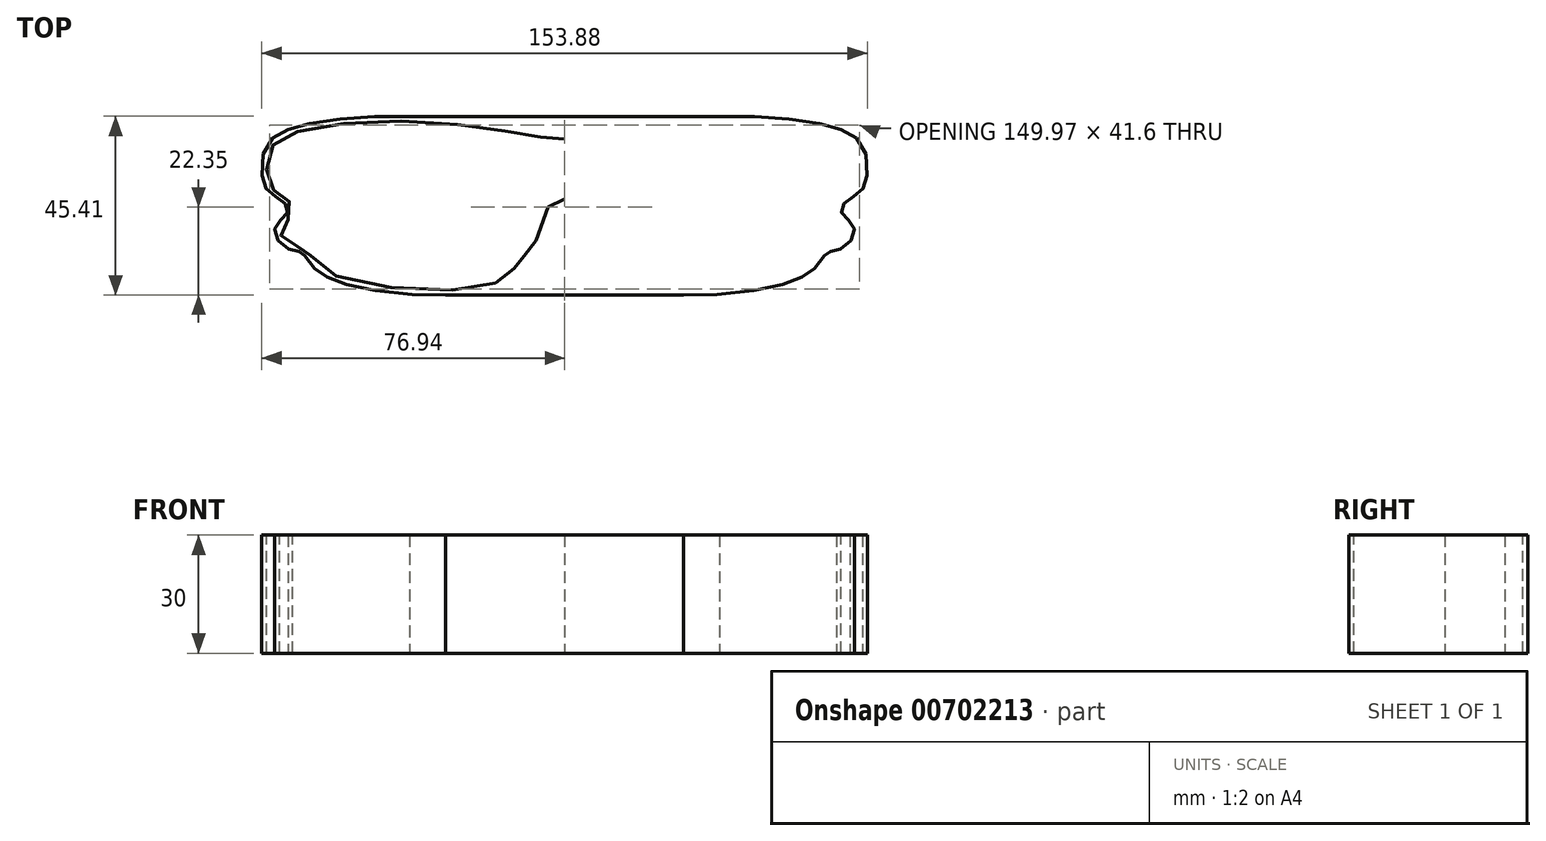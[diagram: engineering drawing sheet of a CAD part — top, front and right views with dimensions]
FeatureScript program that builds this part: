
annotation { "Feature Type Name" : "Feature", "Feature Type Description" : "" }
export const myFeature = defineFeature(function(context is Context, id is Id, definition is map)
    precondition{}
    {
        {
            var Q0;
            Q0=qCreatedBy(makeId("Top.planeOp"),FACE);
            var sketch = newSketch(context, id + "F0", { "sketchPlane" : qUnion([Q0])});
            skPoint(sketch, "E0", {"position": v(0, 65.63) * mm});
            skPoint(sketch, "E1", {"position": v(87.5, 0) * mm});
            skLineSegment(sketch, "E2", {"start": v(0, 89.37) * mm, "end": v(0, -72.57) * mm, "construction": true});
            skLineSegment(sketch, "E3", {"start": v(-93.15, 0) * mm, "end": v(109.27, 0) * mm, "construction": true});
            skLineSegment(sketch, "E4", {"start": v(36.39, -17.94) * mm, "end": v(36.39, 15.86) * mm, "construction": true});
            skFitSpline(sketch, "E5", {"points": [v(0, 16.42) * mm, v(-8.35, 17.29) * mm, v(-36.63, 20.8) * mm, v(-70.08, 17.58) * mm, v(-75.27, 12.4) * mm, v(-74.68, 4.18) * mm, v(-71.26, 1.93) * mm, v(-69.2, -2.67) * mm, v(-72.43, -6.58) * mm, v(-69.3, -10.6) * mm, v(-66.17, -11.28) * mm, v(-60.79, -17.05) * mm, v(-22.15, -21.36) * mm, v(-13.05, -16.95) * mm, v(-10.8, -13.53) * mm, v(-8.84, -12.65) * mm, v(-3.88, -0.47) * mm, v(0, 1.2) * mm], "startDerivative": vector(-129.58, 0) * mm, "endDerivative": vector(103.17, 3.03) * mm});
            skFitSpline(sketch, "E6.MirrorCS", {"points": [v(0, 16.42) * mm, v(8.35, 17.29) * mm, v(36.63, 20.8) * mm, v(70.08, 17.58) * mm, v(75.27, 12.4) * mm, v(74.68, 4.18) * mm, v(71.26, 1.93) * mm, v(69.2, -2.67) * mm, v(72.43, -6.58) * mm, v(69.3, -10.6) * mm, v(66.17, -11.28) * mm, v(60.79, -17.05) * mm, v(22.15, -21.36) * mm, v(13.05, -16.95) * mm, v(10.8, -13.53) * mm, v(8.84, -12.65) * mm, v(3.88, -0.47) * mm, v(0, 1.2) * mm], "startDerivative": vector(129.58, 0) * mm, "endDerivative": vector(-103.17, 3.03) * mm});
            skFitSpline(sketch, "E7.0", {"points": [v(0, 17.62) * mm, v(-0.65, 17.62) * mm, v(-1.94, 17.66) * mm, v(-4.04, 17.86) * mm, v(-6.04, 18.13) * mm, v(-7.86, 18.42) * mm, v(-9.86, 18.75) * mm, v(-12.67, 19.23) * mm, v(-16.5, 19.86) * mm, v(-20.74, 20.5) * mm, v(-25.33, 21.1) * mm, v(-30.22, 21.62) * mm, v(-35.38, 21.98) * mm, v(-40.74, 22.15) * mm, v(-46.18, 22.12) * mm, v(-51.54, 21.9) * mm, v(-56.68, 21.48) * mm, v(-61.46, 20.9) * mm, v(-65.01, 20.25) * mm, v(-67.54, 19.65) * mm, v(-69.26, 19.16) * mm, v(-70.8, 18.61) * mm, v(-72.13, 18) * mm, v(-73.3, 17.32) * mm, v(-74.29, 16.52) * mm, v(-75.12, 15.6) * mm, v(-75.98, 14.2) * mm, v(-76.64, 12.2) * mm, v(-76.92, 9.87) * mm, v(-76.9, 8) * mm, v(-76.78, 6.63) * mm, v(-76.56, 5.56) * mm, v(-76.31, 4.76) * mm, v(-76.08, 4.2) * mm, v(-75.8, 3.66) * mm, v(-75.44, 3.17) * mm, v(-75.04, 2.77) * mm, v(-74.48, 2.32) * mm, v(-73.79, 1.94) * mm, v(-73.03, 1.59) * mm, v(-72.49, 1.3) * mm, v(-72.1, 1.06) * mm, v(-71.71, 0.77) * mm, v(-71.23, 0.29) * mm, v(-70.74, -0.4) * mm, v(-70.45, -0.98) * mm, v(-70.31, -1.41) * mm, v(-70.26, -1.7) * mm, v(-70.26, -1.96) * mm, v(-70.3, -2.16) * mm, v(-70.35, -2.32) * mm, v(-70.48, -2.54) * mm, v(-70.68, -2.8) * mm, v(-71.05, -3.17) * mm, v(-71.53, -3.59) * mm, v(-72.05, -4.04) * mm, v(-72.45, -4.4) * mm, v(-72.83, -4.82) * mm, v(-73.2, -5.3) * mm, v(-73.44, -5.77) * mm, v(-73.58, -6.2) * mm, v(-73.67, -6.68) * mm, v(-73.66, -7.24) * mm, v(-73.52, -7.88) * mm, v(-73.28, -8.46) * mm, v(-72.87, -9.2) * mm, v(-72.22, -10.01) * mm, v(-71.44, -10.71) * mm, v(-70.77, -11.18) * mm, v(-70.33, -11.44) * mm, v(-69.97, -11.61) * mm, v(-69.6, -11.77) * mm, v(-69.16, -11.91) * mm, v(-68.66, -12.02) * mm, v(-68.05, -12.1) * mm, v(-67.55, -12.14) * mm, v(-67.19, -12.18) * mm, v(-66.99, -12.22) * mm, v(-66.88, -12.26) * mm, v(-66.82, -12.29) * mm, v(-66.77, -12.32) * mm, v(-66.67, -12.4) * mm, v(-66.5, -12.57) * mm, v(-66.3, -12.83) * mm, v(-65.99, -13.26) * mm, v(-65.53, -13.97) * mm, v(-64.83, -14.97) * mm, v(-63.92, -16.06) * mm, v(-62.95, -16.98) * mm, v(-62.01, -17.7) * mm, v(-61.23, -18.2) * mm, v(-60.37, -18.68) * mm, v(-59.13, -19.27) * mm, v(-57.42, -19.95) * mm, v(-55.13, -20.65) * mm, v(-51.82, -21.47) * mm, v(-47.27, -22.27) * mm, v(-41.45, -22.9) * mm, v(-35.56, -23.22) * mm, v(-30.86, -23.23) * mm, v(-27.36, -23.09) * mm, v(-24.9, -22.9) * mm, v(-22.65, -22.66) * mm, v(-20.65, -22.34) * mm, v(-18.88, -21.94) * mm, v(-16.82, -21.3) * mm, v(-15.14, -20.51) * mm, v(-13.78, -19.54) * mm, v(-12.92, -18.74) * mm, v(-12.32, -18) * mm, v(-11.9, -17.4) * mm, v(-11.52, -16.8) * mm, v(-11.13, -16.06) * mm, v(-10.79, -15.43) * mm, v(-10.55, -15.03) * mm, v(-10.39, -14.79) * mm, v(-10.25, -14.62) * mm, v(-10.18, -14.56) * mm, v(-10.16, -14.55) * mm, v(-10.16, -14.54) * mm, v(-10.1, -14.52) * mm, v(-9.92, -14.47) * mm, v(-9.63, -14.41) * mm, v(-9.25, -14.31) * mm, v(-8.78, -14.12) * mm, v(-8.38, -13.86) * mm, v(-8.08, -13.6) * mm, v(-7.8, -13.28) * mm, v(-7.5, -12.86) * mm, v(-7.18, -12.3) * mm, v(-6.9, -11.69) * mm, v(-6.52, -10.8) * mm, v(-6.09, -9.56) * mm, v(-5.57, -7.95) * mm, v(-5.05, -6.3) * mm, v(-4.51, -4.68) * mm, v(-4.06, -3.44) * mm, v(-3.68, -2.56) * mm, v(-3.4, -1.98) * mm, v(-3.12, -1.48) * mm, v(-2.86, -1.09) * mm, v(-2.6, -0.8) * mm, v(-2.28, -0.5) * mm, v(-1.9, -0.27) * mm, v(-1.37, -0.11) * mm, v(-0.74, -0.03) * mm, v(-0.23, -0.02) * mm, v(0.04, 0) * mm]});
            skFitSpline(sketch, "E7.1", {"points": [v(0, 17.62) * mm, v(0.65, 17.62) * mm, v(1.94, 17.66) * mm, v(4.04, 17.86) * mm, v(6.04, 18.13) * mm, v(7.86, 18.42) * mm, v(9.86, 18.75) * mm, v(12.67, 19.23) * mm, v(16.5, 19.86) * mm, v(20.74, 20.5) * mm, v(25.33, 21.1) * mm, v(30.22, 21.62) * mm, v(35.38, 21.98) * mm, v(40.74, 22.15) * mm, v(46.18, 22.12) * mm, v(51.54, 21.9) * mm, v(56.68, 21.48) * mm, v(61.46, 20.9) * mm, v(65.01, 20.25) * mm, v(67.54, 19.65) * mm, v(69.26, 19.16) * mm, v(70.8, 18.61) * mm, v(72.13, 18) * mm, v(73.3, 17.32) * mm, v(74.29, 16.52) * mm, v(75.12, 15.6) * mm, v(75.98, 14.2) * mm, v(76.64, 12.2) * mm, v(76.92, 9.87) * mm, v(76.9, 8) * mm, v(76.78, 6.63) * mm, v(76.56, 5.56) * mm, v(76.31, 4.76) * mm, v(76.08, 4.2) * mm, v(75.8, 3.66) * mm, v(75.44, 3.17) * mm, v(75.04, 2.77) * mm, v(74.48, 2.32) * mm, v(73.79, 1.94) * mm, v(73.03, 1.59) * mm, v(72.49, 1.3) * mm, v(72.1, 1.06) * mm, v(71.71, 0.77) * mm, v(71.23, 0.29) * mm, v(70.74, -0.4) * mm, v(70.45, -0.98) * mm, v(70.31, -1.41) * mm, v(70.26, -1.7) * mm, v(70.26, -1.96) * mm, v(70.3, -2.16) * mm, v(70.35, -2.32) * mm, v(70.48, -2.54) * mm, v(70.68, -2.8) * mm, v(71.05, -3.17) * mm, v(71.53, -3.59) * mm, v(72.05, -4.04) * mm, v(72.45, -4.4) * mm, v(72.83, -4.82) * mm, v(73.2, -5.3) * mm, v(73.44, -5.77) * mm, v(73.58, -6.2) * mm, v(73.67, -6.68) * mm, v(73.66, -7.24) * mm, v(73.52, -7.88) * mm, v(73.28, -8.46) * mm, v(72.87, -9.2) * mm, v(72.22, -10.01) * mm, v(71.44, -10.71) * mm, v(70.77, -11.18) * mm, v(70.33, -11.44) * mm, v(69.97, -11.61) * mm, v(69.6, -11.77) * mm, v(69.16, -11.91) * mm, v(68.66, -12.02) * mm, v(68.05, -12.1) * mm, v(67.55, -12.14) * mm, v(67.19, -12.18) * mm, v(66.99, -12.22) * mm, v(66.88, -12.26) * mm, v(66.82, -12.29) * mm, v(66.77, -12.32) * mm, v(66.67, -12.4) * mm, v(66.5, -12.57) * mm, v(66.3, -12.83) * mm, v(65.99, -13.26) * mm, v(65.53, -13.97) * mm, v(64.83, -14.97) * mm, v(63.92, -16.06) * mm, v(62.95, -16.98) * mm, v(62.01, -17.7) * mm, v(61.23, -18.2) * mm, v(60.37, -18.68) * mm, v(59.13, -19.27) * mm, v(57.42, -19.95) * mm, v(55.13, -20.65) * mm, v(51.82, -21.47) * mm, v(47.27, -22.27) * mm, v(41.45, -22.9) * mm, v(35.56, -23.22) * mm, v(30.86, -23.23) * mm, v(27.36, -23.09) * mm, v(24.9, -22.9) * mm, v(22.65, -22.66) * mm, v(20.65, -22.34) * mm, v(18.88, -21.94) * mm, v(16.82, -21.3) * mm, v(15.14, -20.51) * mm, v(13.78, -19.54) * mm, v(12.92, -18.74) * mm, v(12.32, -18) * mm, v(11.9, -17.4) * mm, v(11.52, -16.8) * mm, v(11.13, -16.06) * mm, v(10.79, -15.43) * mm, v(10.55, -15.03) * mm, v(10.39, -14.79) * mm, v(10.25, -14.62) * mm, v(10.18, -14.56) * mm, v(10.16, -14.55) * mm, v(10.16, -14.54) * mm, v(10.1, -14.52) * mm, v(9.92, -14.47) * mm, v(9.63, -14.41) * mm, v(9.25, -14.31) * mm, v(8.78, -14.12) * mm, v(8.38, -13.86) * mm, v(8.08, -13.6) * mm, v(7.8, -13.28) * mm, v(7.5, -12.86) * mm, v(7.18, -12.3) * mm, v(6.9, -11.69) * mm, v(6.52, -10.8) * mm, v(6.09, -9.56) * mm, v(5.57, -7.95) * mm, v(5.05, -6.3) * mm, v(4.51, -4.68) * mm, v(4.06, -3.44) * mm, v(3.68, -2.56) * mm, v(3.4, -1.98) * mm, v(3.12, -1.48) * mm, v(2.86, -1.09) * mm, v(2.6, -0.8) * mm, v(2.28, -0.5) * mm, v(1.9, -0.27) * mm, v(1.37, -0.11) * mm, v(0.74, -0.03) * mm, v(0.23, -0.02) * mm, v(-0.04, 0) * mm]});
            skLineSegment(sketch, "E8", {"start": v(-32.54, -23.21) * mm, "end": v(32.54, -23.21) * mm});
            skLineSegment(sketch, "E9", {"start": v(-42.57, 22.13) * mm, "end": v(42.57, 22.13) * mm});
            skSolve(sketch);
        }
        {
            var Q0;
            Q0 = qSketchRegion(id + "F0", true);
            extrude(context, id + "F1", {"entities" : qUnion([Q0]), "depth" : 30 * mm, "offsetDistance" : 25 * mm});
        }
    });
